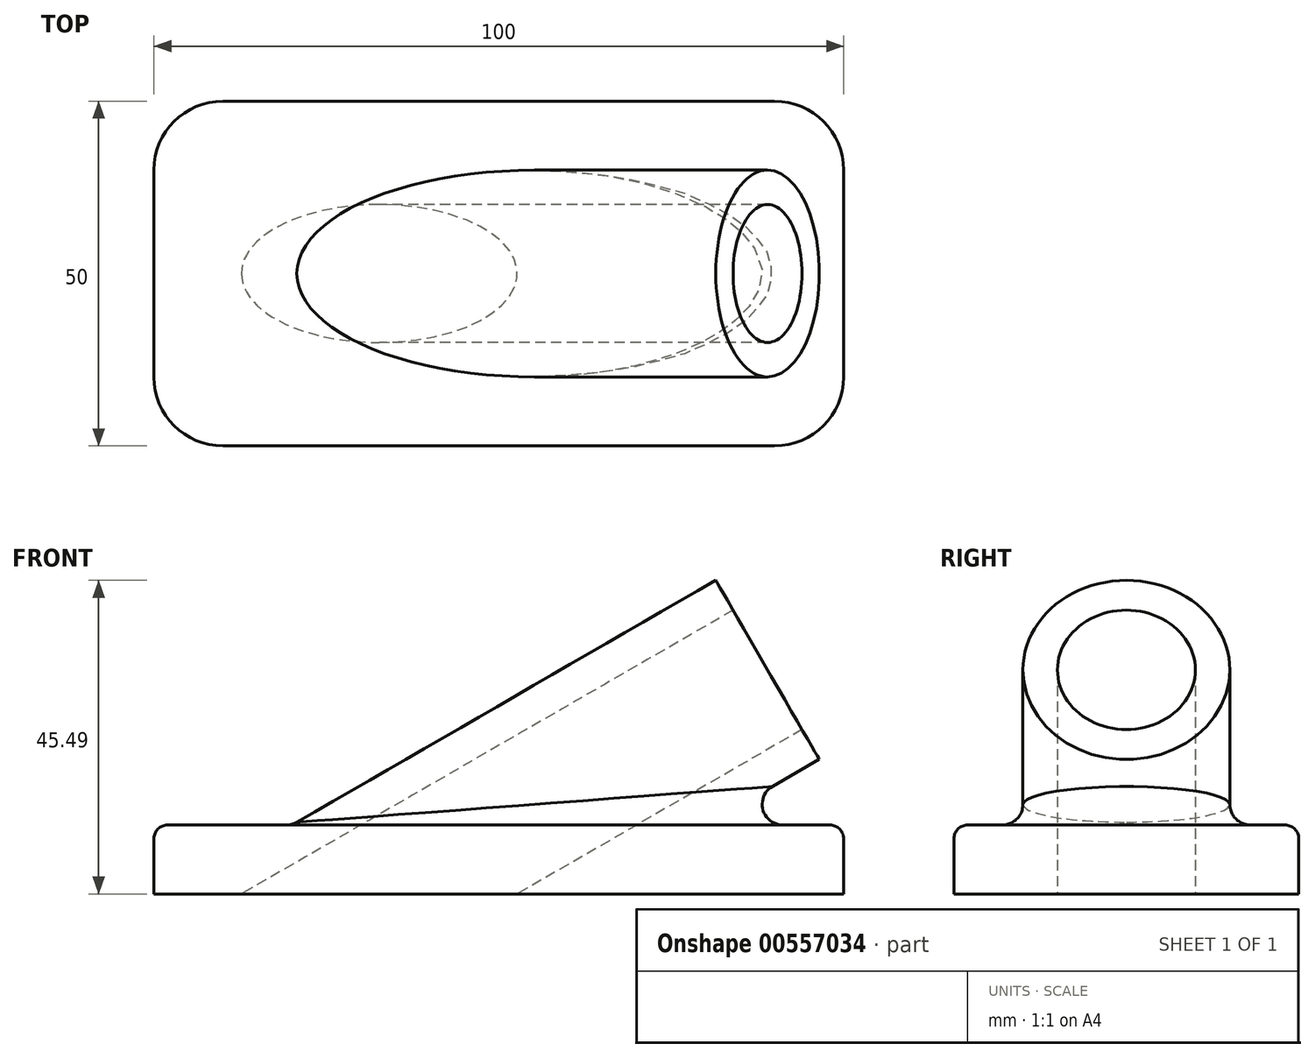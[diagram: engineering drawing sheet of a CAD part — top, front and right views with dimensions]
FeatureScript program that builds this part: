
annotation { "Feature Type Name" : "Feature", "Feature Type Description" : "" }
export const myFeature = defineFeature(function(context is Context, id is Id, definition is map)
    precondition{}
    {
        {
            assignVariable(context, id + "F0", {"name" : "b", "anyValue" : 30});
        }
        {
            var Q0;
            Q0=qCreatedBy(makeId("Top.planeOp"),FACE);
            var sketch = newSketch(context, id + "F1", { "sketchPlane" : qUnion([Q0])});
            skLineSegment(sketch, "E0.bottom", {"start": v(0, 0) * mm, "end": v(100, 0) * mm});
            skLineSegment(sketch, "E0.top", {"start": v(0, 50) * mm, "end": v(100, 50) * mm});
            skLineSegment(sketch, "E0.left", {"start": v(0, 0) * mm, "end": v(0, 50) * mm});
            skLineSegment(sketch, "E0.right", {"start": v(100, 0) * mm, "end": v(100, 50) * mm});
            skSolve(sketch);
        }
        {
            var Q0;
            Q0 = qSketchRegion(id + "F1", true);
            extrude(context, id + "F2", {"entities" : qUnion([Q0]), "depth" : 10 * mm, "offsetDistance" : 25 * mm});
        }
        {
            var Q0;
            Q0=makeQuery(id+"F2.opExtrude","CAP_FACE",FACE,{"disambiguationData":[OSD([sQuery(id+"F1.wireOp",EDGE,"E0.bottom"),sQuery(id+"F1.wireOp",EDGE,"E0.top"),sQuery(id+"F1.wireOp",EDGE,"E0.left"),sQuery(id+"F1.wireOp",EDGE,"E0.right")])],"isStart":false});
            var sketch = newSketch(context, id + "F3", { "sketchPlane" : qUnion([Q0])});
            skLineSegment(sketch, "E1", {"start": v(50, 50) * mm, "end": v(50, 0) * mm});
            skLineSegment(sketch, "E2", {"start": v(0, 25) * mm, "end": v(100, 25) * mm});
            skSolve(sketch);
        }
        {
            var Q0;
            Q0=sQuery(id+"F3.wireOp",EDGE,"E1");
            cPlane(context, id + "F4", {"entities" : qUnion([Q0]), "cplaneType" : CPlaneType.LINE_ANGLE, "offset" : 25 * mm, "angle" : (getVariable(context, 'b')) * degree, "width" : 150 * mm, "height" : 150 * mm});
        }
        {
            var Q0;
            Q0=qCreatedBy(id+"F4.planeOp",FACE);
            var sketch = newSketch(context, id + "F5", { "sketchPlane" : qUnion([Q0])});
            skLineSegment(sketch, "E3", {"start": v(-9.6, -25) * mm, "end": v(105.9, -25) * mm});
            skLineSegment(sketch, "E4", {"start": v(-2.63, -25) * mm, "end": v(-2.63, -40) * mm});
            skLineSegment(sketch, "E5", {"start": v(-2.63, -40) * mm, "end": v(93.3, -40) * mm});
            skLineSegment(sketch, "E6", {"start": v(93.3, -40) * mm, "end": v(93.3, -25) * mm});
            skSolve(sketch);
        }
        {
            var Q0;
            Q0 = qSketchRegion(id + "F5", true);
            var Q1;
            Q1=sQuery(id+"F5.wireOp",EDGE,"E3");
            revolve(context, id + "F6", {"operationType" : NewBodyOperationType.ADD, "entities" : qUnion([Q0]), "axis" : qUnion([Q1]), "revolveType" : RevolveType.FULL});
        }
        {
            var Q0;
            Q0=makeQuery(id+"F6.opRevolve","SWEPT_FACE",FACE,{"disambiguationData":[OSD([sQuery(id+"F5.wireOp",EDGE,"E6")])]});
            shell(context, id + "F7", {"entities" : qUnion([Q0]), "thickness" : 5 * mm});
        }
        {
            var Q0;
            Q0=makeQuery(id+"F6.opRevolve","SWEPT_FACE",FACE,{"disambiguationData":[OSD([sQuery(id+"F5.wireOp",EDGE,"E4")])]});
            var Q1;
            Q1=makeQuery(id+"F2.opExtrude","CAP_FACE",FACE,{"disambiguationData":[OSD([sQuery(id+"F1.wireOp",EDGE,"E0.bottom"),sQuery(id+"F1.wireOp",EDGE,"E0.top"),sQuery(id+"F1.wireOp",EDGE,"E0.left"),sQuery(id+"F1.wireOp",EDGE,"E0.right")])],"isStart":true});
            extrude(context, id + "F8", {"entities" : qUnion([Q0]), "operationType" : NewBodyOperationType.REMOVE, "endBound" : BoundingType.UP_TO_SURFACE, "oppositeDirection" : true, "depth" : 25 * mm, "endBoundEntityFace" : qUnion([Q1]), "offsetDistance" : 25 * mm});
        }
        {
            var Q0;
            Q0=makeQuery(id+"F6.boolean.opBoolean","INTERSECT",EDGE,{"derivedFrom":[makeQuery(id+"F2.opExtrude","CAP_FACE",FACE,{"disambiguationData":[OSD([sQuery(id+"F1.wireOp",EDGE,"E0.bottom"),sQuery(id+"F1.wireOp",EDGE,"E0.top"),sQuery(id+"F1.wireOp",EDGE,"E0.left"),sQuery(id+"F1.wireOp",EDGE,"E0.right")])],"isStart":false}),makeQuery(id+"F6.opRevolve","SWEPT_FACE",FACE,{"disambiguationData":[OSD([sQuery(id+"F5.wireOp",EDGE,"E5")])]})]});
            fillet(context, id + "F9", {"entities" : qUnion([Q0]), "radius" : 3 * mm, "tangentPropagation" : true, "allowEdgeOverflow" : false});
        }
        {
            var Q0;
            Q0=makeQuery(id+"F2.opExtrude","SWEPT_EDGE",EDGE,{"disambiguationData":[OSD([sQuery(id+"F1.wireOp",EDGE,"E0.bottom"),sQuery(id+"F1.wireOp",EDGE,"E0.left")])]});
            var Q1;
            Q1=makeQuery(id+"F2.opExtrude","SWEPT_EDGE",EDGE,{"disambiguationData":[OSD([sQuery(id+"F1.wireOp",EDGE,"E0.bottom"),sQuery(id+"F1.wireOp",EDGE,"E0.right")])]});
            var Q2;
            Q2=makeQuery(id+"F2.opExtrude","SWEPT_EDGE",EDGE,{"disambiguationData":[OSD([sQuery(id+"F1.wireOp",EDGE,"E0.top"),sQuery(id+"F1.wireOp",EDGE,"E0.left")])]});
            var Q3;
            Q3=makeQuery(id+"F2.opExtrude","SWEPT_EDGE",EDGE,{"disambiguationData":[OSD([sQuery(id+"F1.wireOp",EDGE,"E0.top"),sQuery(id+"F1.wireOp",EDGE,"E0.right")])]});
            fillet(context, id + "F10", {"entities" : qUnion([Q0, Q1, Q2, Q3]), "radius" : 10 * mm, "tangentPropagation" : true, "allowEdgeOverflow" : false});
        }
        {
            var Q0;
            Q0=makeQuery(id+"F2.opExtrude","CAP_EDGE",EDGE,{"disambiguationData":[OSD([sQuery(id+"F1.wireOp",EDGE,"E0.bottom")])],"isStart":false});
            fillet(context, id + "F11", {"entities" : qUnion([Q0]), "radius" : 2 * mm, "tangentPropagation" : true, "allowEdgeOverflow" : false});
        }
    });
